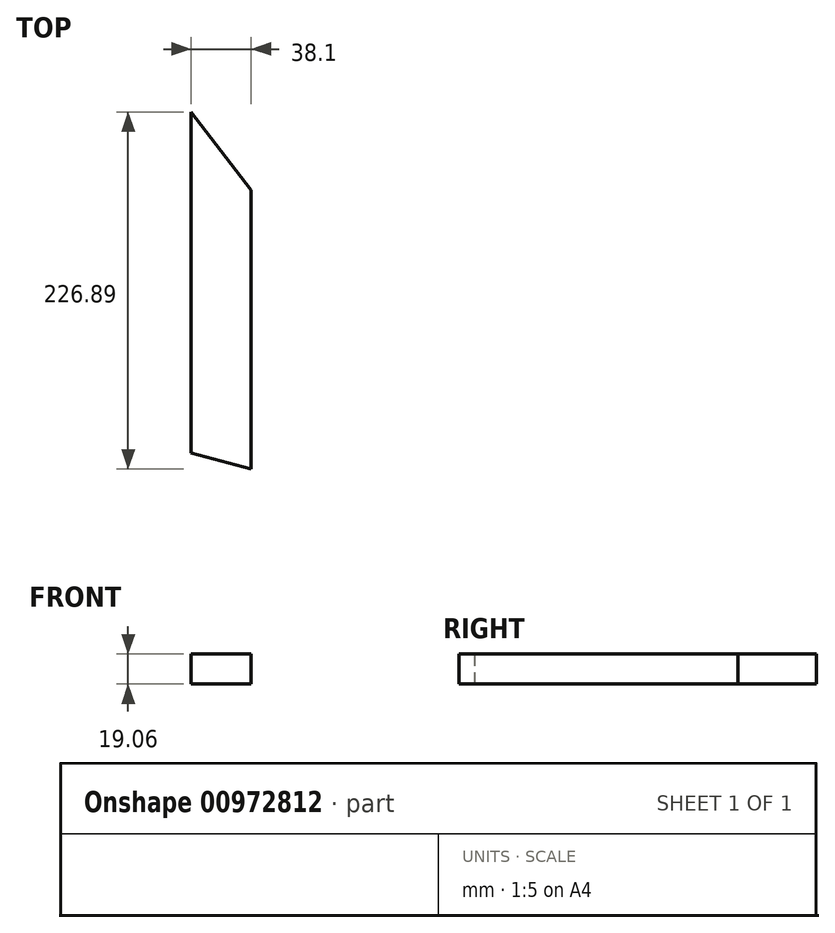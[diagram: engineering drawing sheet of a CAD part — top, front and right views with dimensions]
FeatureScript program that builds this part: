
annotation { "Feature Type Name" : "Feature", "Feature Type Description" : "" }
export const myFeature = defineFeature(function(context is Context, id is Id, definition is map)
    precondition{}
    {
        {
            var Q0;
            Q0=qCreatedBy(makeId("Front.planeOp"),FACE);
            var sketch = newSketch(context, id + "F0", { "sketchPlane" : qUnion([Q0])});
            skLineSegment(sketch, "E0.bottom", {"start": v(-19.05, 9.52) * mm, "end": v(19.05, 9.52) * mm});
            skLineSegment(sketch, "E0.top", {"start": v(-19.05, -9.52) * mm, "end": v(19.05, -9.52) * mm});
            skLineSegment(sketch, "E0.left", {"start": v(-19.05, 9.52) * mm, "end": v(-19.05, -9.52) * mm});
            skLineSegment(sketch, "E0.right", {"start": v(19.05, 9.52) * mm, "end": v(19.05, -9.52) * mm});
            skPoint(sketch, "E0.middle", {"position": v(0, 0) * mm});
            skSolve(sketch);
        }
        {
            var Q0;
            Q0=makeQuery(id+"F0.imprint","IMPRINT",FACE,{"disambiguationData":[TD([[makeQuery(id+"F0.imprint","IMPRINT",EDGE,{"derivedFrom":sQuery(id+"F0.wireOp",EDGE,"E0.bottom")}),-1.0]])]});
            extrude(context, id + "F1", {"entities" : qUnion([Q0]), "depth" : 508 * mm, "offsetDistance" : 25.4 * mm});
        }
        {
            var Q0;
            Q0=makeQuery(id+"F1.opExtrude","SWEPT_FACE",FACE,{"disambiguationData":[OSD([sQuery(id+"F0.wireOp",EDGE,"E0.bottom")])]});
            var sketch = newSketch(context, id + "F2", { "sketchPlane" : qUnion([Q0])});
            skLineSegment(sketch, "E1", {"start": v(-19.05, 0) * mm, "end": v(19.05, -49.65) * mm});
            skLineSegment(sketch, "E2", {"start": v(19.05, -49.65) * mm, "end": v(19.05, 0) * mm});
            skLineSegment(sketch, "E3", {"start": v(19.05, 0) * mm, "end": v(-19.05, 0) * mm});
            skLineSegment(sketch, "E4", {"start": v(-19.05, 0) * mm, "end": v(-228.35, -160.6) * mm, "construction": true});
            skLineSegment(sketch, "E5", {"start": v(19.05, -483.02) * mm, "end": v(228.35, -322.42) * mm, "construction": true});
            skLineSegment(sketch, "E6", {"start": v(19.05, -483.02) * mm, "end": v(19.05, -508) * mm});
            skLineSegment(sketch, "E7", {"start": v(19.05, -508) * mm, "end": v(-19.05, -508) * mm});
            skLineSegment(sketch, "E8", {"start": v(-228.35, -160.6) * mm, "end": v(-190.25, -210.25) * mm, "construction": true});
            skLineSegment(sketch, "E9", {"start": v(-190.25, -210.25) * mm, "end": v(228.35, -322.42) * mm, "construction": true});
            skLineSegment(sketch, "E10", {"start": v(228.35, -322.42) * mm, "end": v(190.25, -272.77) * mm, "construction": true});
            skLineSegment(sketch, "E11", {"start": v(190.25, -272.77) * mm, "end": v(-228.35, -160.6) * mm, "construction": true});
            skLineSegment(sketch, "E12", {"start": v(-19.05, -256.13) * mm, "end": v(-19.05, -508) * mm});
            skLineSegment(sketch, "E13", {"start": v(19.05, -266.34) * mm, "end": v(19.05, -483.02) * mm});
            skLineSegment(sketch, "E14", {"start": v(19.05, -483.02) * mm, "end": v(-19.05, -433.37) * mm, "construction": true});
            skLineSegment(sketch, "E15", {"start": v(-19.05, -256.13) * mm, "end": v(-19.05, -216.68) * mm});
            skLineSegment(sketch, "E16", {"start": v(-19.05, -216.68) * mm, "end": v(19.05, -226.9) * mm});
            skLineSegment(sketch, "E17", {"start": v(19.05, -226.9) * mm, "end": v(19.05, -266.34) * mm});
            skLineSegment(sketch, "E18", {"start": v(-19.05, -508) * mm, "end": v(-19.05, -433.37) * mm});
            skSolve(sketch);
        }
        {
            var Q0;
            Q0=makeQuery(id+"F2.imprint","IMPRINT",FACE,{"disambiguationData":[TD([[makeQuery(id+"F2.imprint","IMPRINT",EDGE,{"derivedFrom":sQuery(id+"F2.wireOp",EDGE,"E1")}),1.0]])]});
            var Q1;
            Q1=makeQuery(id+"F2.imprint","IMPRINT",FACE,{"disambiguationData":[TD([[makeQuery(id+"F2.imprint","IMPRINT",EDGE,{"derivedFrom":sQuery(id+"F2.wireOp",EDGE,"E6")}),1.0]])]});
            extrude(context, id + "F3", {"entities" : qUnion([Q0, Q1]), "operationType" : NewBodyOperationType.REMOVE, "endBound" : BoundingType.THROUGH_ALL, "oppositeDirection" : true, "depth" : 25.4 * mm, "offsetDistance" : 25.4 * mm});
        }
    });
